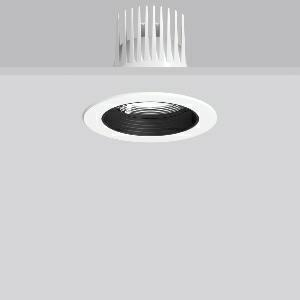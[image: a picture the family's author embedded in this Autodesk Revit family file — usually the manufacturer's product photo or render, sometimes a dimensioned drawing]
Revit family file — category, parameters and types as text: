
# Revit family: heledon_maxi_e_901761_002_2_76_c48b
name_source: partatom
category: Lighting Fixtures
units: mm (PartAtom-declared; Revit-internal decimal feet)

## family parameters
Cut with Voids When Loaded = No
Host = Face
Light Source = No
Part Type = Normal
Room Calculation Point = No
Round Connector Dimension = Use Diameter
Shared = No

## types (1)
- HELEDON maxi E (1 x LED Modul 927, 2550 lm, 2700)
    Apparent Load = 25 VA
    Approval mark = CE
    CIE Flux Codes = 96 100 100 100 100
    Color Rendering = 92
    Color Temperature = 2700
    Default Elevation = 1800 mm
    Description = Series: HELEDON maxi
Round recessed downlight. Housing: die-cast aluminium, powder-coated. Black plastic ring and recessed LED to prevent glare from the side. Optical assembly with lens made of plastic (polycarbonate) for the best homogeneous light distribution - can be changed without tools. Best colour rendering index Ra>90. Suitable for Recessed ceiling mounting. Installation without tools thanks to spring fastening system. Including separate LED converter with connecting cable 600 mm.High quality converter without flickering and stroboscopic effect. Through-wiring box (5 pole) available as accessory. The following accessories can be mounted without use of tools: interchangeable lenses, decorative glasses, honeycomb louvre, clear and frosted diffusers, white interchangeable plastic ring. 
Colour: traffic white, matt (RAL 9016)
Diameter: 162 mm
Height: 3 mm
Cut-out diameter: 152 mm
Recess height: 200 mm
Luminaire: recess height: 135 mm
Lamp: LED
Socket: without socket
Colour temperature: 2700K
Colour rendering index (CRI): 92
System power: 25 W
Rated luminous flux: 2550 lm
Luminous efficiency: 102 lm/W
Control gear: Converter, dimmable, DALI
Protection class: II
Type of protection: IP 20
    Height = 0 mm  [stored 0 ft]
    Lamp = 1 x LED Modul 927
    Lamp Light Flux = 2550 lm
    Lamp count = 1
    Length = 162 mm
    Lifetime = 50000 h
    Luminous efficacy = 102 lm/W
    Manufacturer = RZB
    ModVariant = No
    Model = 901761.002.2.76
    Mounting Place = Ceiling
    Mounting Type = Recessed
    Number of Poles = 1
    OnlyDefault = Yes
    Power Factor = 1
    Product Name = HELEDON maxi E
    Product group = Recessed downlights
    ProductGroupID = 402
    Protection Class = Protection class II
    Protection Degree = IP 20
    RLX_Detail_Level = 1
    RLX_Emergency_Light_Flux = 0 lm
    RLX_Emergency_Type = 0
    RLX_Emergency_Type_DB = No
    RlxData = <blob elided: 119041 chars, md5=7a43ac48>
    Socket = socket
    Standby Power = 0 W
    System Light Flux = 2550 lm
    System Power = 25 W
    Type Comments = Product without accessories
    Type Image = 901663.002.jpg
    URL = http://relux.com
    VarID = ---
    Voltage = 230 V
    Voltage Range = 220-240 V
    Weight = 0.00 kg
    Width = 0 mm  [stored 0 ft]

note: [stored X ft] marks values corroborated as IEEE doubles in the binary element streams (Revit-internal decimal feet)

## geometry (parser evidence)
native form markers: Blend x4, Sweep x11
no freeform markers — native parametric forms only
